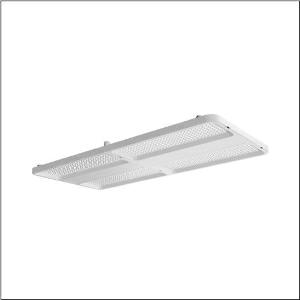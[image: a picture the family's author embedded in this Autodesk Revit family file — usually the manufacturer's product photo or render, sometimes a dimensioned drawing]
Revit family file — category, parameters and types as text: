
# Revit family: highbay_21_maxi_52hn11db6qda
name_source: partatom
category: Lighting Fixtures
units: mm (PartAtom-declared; Revit-internal decimal feet)

## family parameters
Cut with Voids When Loaded = No
Host = Face
Light Source = No
Part Type = Normal
Room Calculation Point = No
Round Connector Dimension = Use Diameter
Shared = No

## types (1)
- --- (1 x LED, 5650 lm, 31.4 W, 6500K)
    Apparent Load = 31 VA
    CIE Flux Codes = 89 97 99 100 100
    Color Rendering = 80
    Color Temperature = 6500K
    Default Elevation = 1800 mm
    Description = high bay luminaire Highbay 21 maxi; direct symmetric narrow distribution, light control with lens of PMMA; UGR ≤ 22 (X = 4H | Y = 8H | S = 0.25H | reflection values 70/50/20); luminous flux: 36.840lm; light colour: 865, colour temperature: 6500K, MacAdam ≤ 3 SDCM (initial), colour rendering: CRI > 80; luminous efficacy: 186,3lm/W; rated service life: 75.000h (L80) at AT= ta max; control: DALI 2; luminaire connection: terminal, 5-pole, max. 2.5mm² (cable entry for one cable, Ø 8.5..16mm); mains connection: 230..240V, AC/DC 0/50..60Hz; connected load: 197,7W; protection rating (complete): IP66; insulation class (complete): insulation class I (protective earthing); protection symbol: D; impact resistance: IK08; certification: CE, ENEC, VDE, UKCA; luminaire for central battery installations according to EN 60598-2-22, internal wiring halogen-free; luminaire LABS conformity tested according to VDMA 24364:2018-05; Suitable for use in the food industry according to the specifications of IFS-Food, HACCP and/or BRC; housing frame of high-performance plastic PA6, matt traffic white (RAL 9016); cover of PMMA; dimension (LxWxH): 946 x 442 x 72mm; permissible operating ambient temperature: -40..+60°C (reducing of maximum allowable ambient temperature of 5°C with ceiling mounting); packaging unit: 1 piece; (delivery without accessories; please order mounting accessories separately)
    Height = 72 mm  [stored 0.23622 ft]
    Lamp = 1 x LED
    Lamp Light Flux = 5650 lm
    Lamp Power = 31.4 W
    Lamp count = 1
    Length = 946 mm
    Luminous efficacy = 180 lm/W
    Manufacturer = Siteco
    ModVariant = No
    Model = 52HN11DB6QDA
    Mounting Place = Ceiling
    Mounting Type = Pendant
    Number of Poles = 1
    OnlyDefault = Yes
    Power Factor = 1
    Product Name = Highbay 21 maxi
    Product group = high bay luminaire
    ProductGroupID = 902
    Protection Class = Protection class I
    Protection Degree = IP 66
    RLX_Detail_Level = 1
    RLX_Emergency_Light_Flux = 0 lm
    RLX_Emergency_Type = 0
    RLX_Emergency_Type_DB = No
    RlxData = <blob elided: 128477 chars, md5=3c28f145>
    Socket = socket
    Standby Power = 0 W
    System Light Flux = 5650 lm
    System Power = 31 W
    Type Comments = : DC mode (central or group accumulator) initial emergency light level
    Type Image = l_1363244.jpg
    URL = http://relux.com
    VarID = @adj_003295
    Voltage = 0 V
    Weight = 0.00 kg
    Width = 442 mm

note: [stored X ft] marks values corroborated as IEEE doubles in the binary element streams (Revit-internal decimal feet)

## geometry (parser evidence)
native form markers: Blend x4, Sweep x10
no freeform markers — native parametric forms only
